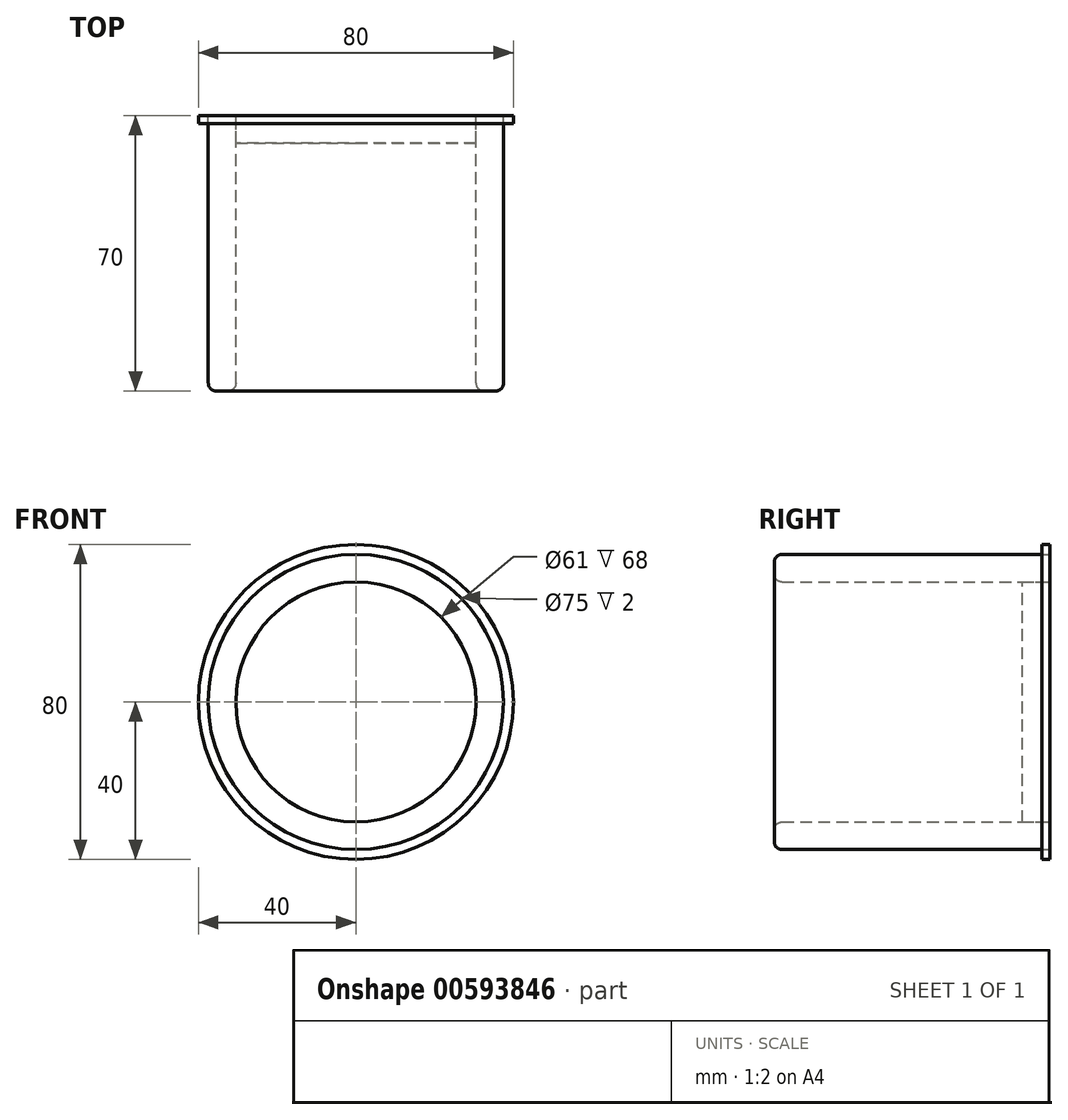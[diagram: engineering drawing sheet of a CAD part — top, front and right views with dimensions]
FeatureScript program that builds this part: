
annotation { "Feature Type Name" : "Feature", "Feature Type Description" : "" }
export const myFeature = defineFeature(function(context is Context, id is Id, definition is map)
    precondition{}
    {
        {
            var Q0;
            Q0=qCreatedBy(makeId("Front.planeOp"),FACE);
            var sketch = newSketch(context, id + "F0", { "sketchPlane" : qUnion([Q0])});
            skCircle(sketch, "E0", {"center": v(0, 0) * mm, "radius": 40 * mm});
            skCircle(sketch, "E1", {"center": v(0, 0) * mm, "radius": 37.5 * mm});
            skCircle(sketch, "E2", {"center": v(0, 0) * mm, "radius": 30.5 * mm});
            skSolve(sketch);
        }
        {
            var Q0;
            Q0 = qSketchRegion(id + "F0", true);
            extrude(context, id + "F1", {"entities" : qUnion([Q0]), "depth" : 2 * mm, "offsetDistance" : 25 * mm});
        }
        {
            var Q0;
            Q0=makeQuery(id+"F0.imprint","IMPRINT",FACE,{"disambiguationData":[TD([[makeQuery(id+"F0.imprint","IMPRINT",EDGE,{"derivedFrom":sQuery(id+"F0.wireOp",EDGE,"E2")}),1.0]])]});
            extrude(context, id + "F2", {"entities" : qUnion([Q0]), "depth" : 7 * mm, "offsetDistance" : 25 * mm});
        }
        {
            var Q0;
            Q0=makeQuery(id+"F0.imprint","IMPRINT",FACE,{"disambiguationData":[TD([[makeQuery(id+"F0.imprint","IMPRINT",EDGE,{"derivedFrom":sQuery(id+"F0.wireOp",EDGE,"E1")}),1.0]])]});
            extrude(context, id + "F3", {"entities" : qUnion([Q0]), "depth" : 70 * mm, "offsetDistance" : 25 * mm});
        }
        {
            var Q0;
            Q0=makeQuery(id+"F3.opExtrude","CAP_EDGE",EDGE,{"disambiguationData":[OSD([sQuery(id+"F0.wireOp",EDGE,"E1")])],"isStart":false});
            fillet(context, id + "F4", {"entities" : qUnion([Q0]), "radius" : 2 * mm, "tangentPropagation" : true, "allowEdgeOverflow" : false});
        }
        {
            var Q0;
            Q0=makeQuery(id+"F3.opExtrude","CAP_EDGE",EDGE,{"disambiguationData":[OSD([sQuery(id+"F0.wireOp",EDGE,"E2")])],"isStart":false});
            fillet(context, id + "F5", {"entities" : qUnion([Q0]), "radius" : 2 * mm, "tangentPropagation" : true, "allowEdgeOverflow" : false});
        }
    });
